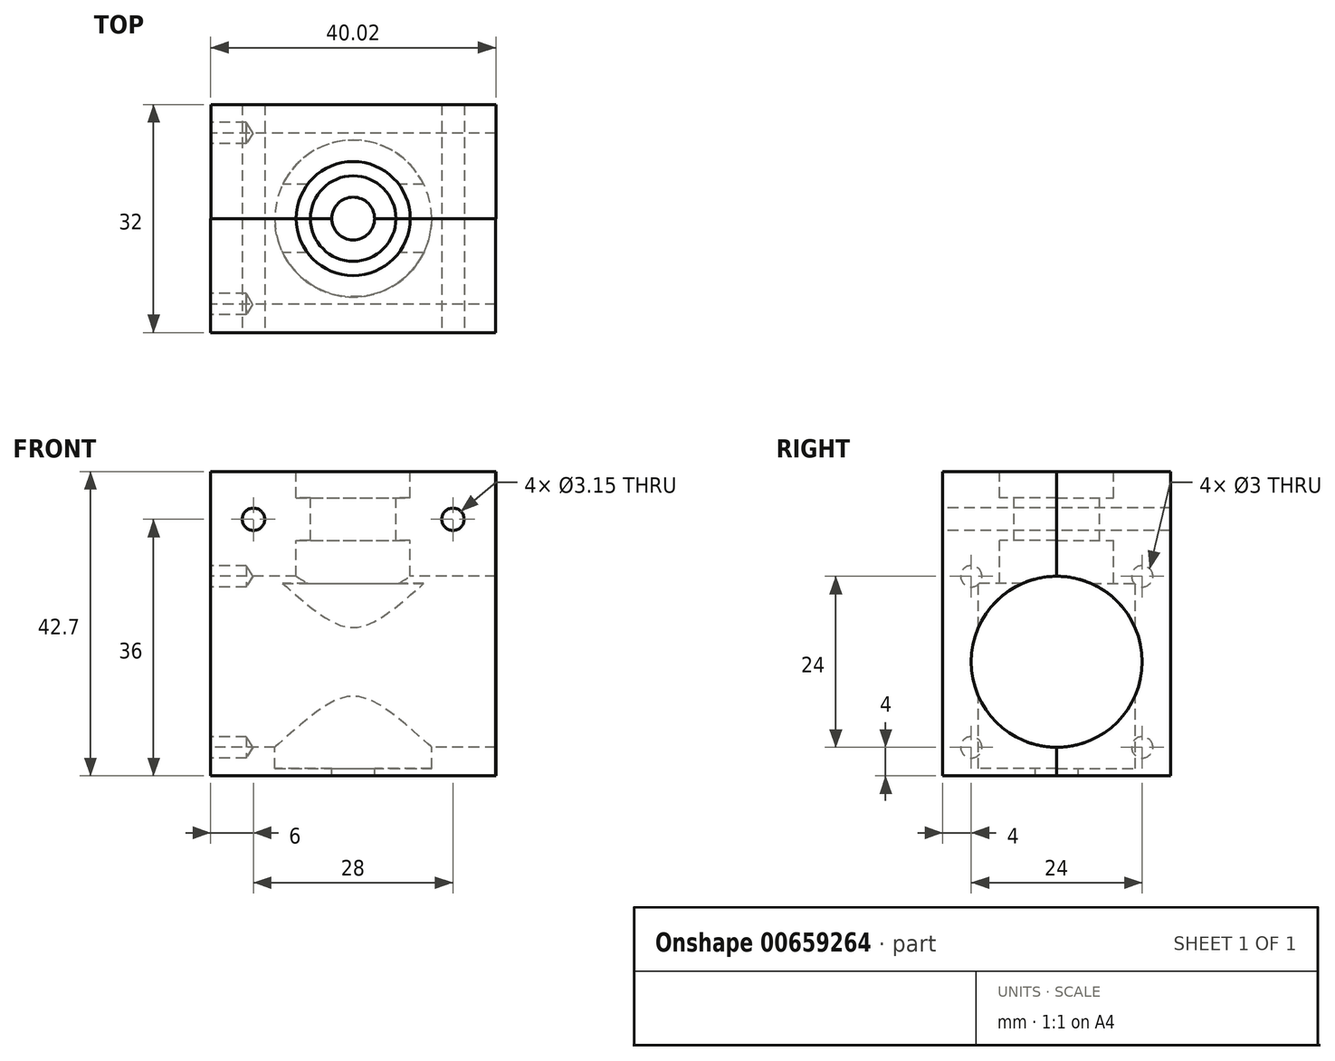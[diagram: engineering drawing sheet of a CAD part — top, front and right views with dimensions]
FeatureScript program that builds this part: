
annotation { "Feature Type Name" : "Feature", "Feature Type Description" : "" }
export const myFeature = defineFeature(function(context is Context, id is Id, definition is map)
    precondition{}
    {
        {
            var Q0;
            Q0=qCreatedBy(makeId("Top.planeOp"),FACE);
            var sketch = newSketch(context, id + "F0", { "sketchPlane" : qUnion([Q0])});
            skLineSegment(sketch, "E0.bottom", {"start": v(20, 8) * mm, "end": v(-20, 8) * mm});
            skLineSegment(sketch, "E0.top", {"start": v(20, -8) * mm, "end": v(-20, -8) * mm});
            skLineSegment(sketch, "E0.left", {"start": v(20, 8) * mm, "end": v(20, -8) * mm});
            skLineSegment(sketch, "E0.right", {"start": v(-20, 8) * mm, "end": v(-20, -8) * mm});
            skPoint(sketch, "E0.middle", {"position": v(0, 0) * mm});
            skSolve(sketch);
        }
        {
            var Q0;
            Q0=makeQuery(id+"F0.imprint","IMPRINT",FACE,{"disambiguationData":[TD([[makeQuery(id+"F0.imprint","IMPRINT",EDGE,{"derivedFrom":sQuery(id+"F0.wireOp",EDGE,"E0.bottom")}),1.0]])]});
            var sketch = newSketch(context, id + "F1", { "sketchPlane" : qUnion([Q0])});
            skLineSegment(sketch, "E1.bottom", {"start": v(-19.98, 8) * mm, "end": v(20.02, 8) * mm});
            skLineSegment(sketch, "E1.top", {"start": v(-19.98, 24) * mm, "end": v(20.02, 24) * mm});
            skLineSegment(sketch, "E1.left", {"start": v(-19.98, 8) * mm, "end": v(-19.98, 24) * mm});
            skLineSegment(sketch, "E1.right", {"start": v(20.02, 8) * mm, "end": v(20.02, 24) * mm});
            skSolve(sketch);
        }
        {
            var Q0;
            Q0=makeQuery(id+"F0.imprint","IMPRINT",FACE,{"disambiguationData":[TD([[makeQuery(id+"F0.imprint","IMPRINT",EDGE,{"derivedFrom":sQuery(id+"F0.wireOp",EDGE,"E0.bottom")}),1.0]])]});
            extrude(context, id + "F2", {"entities" : qUnion([Q0]), "depth" : 42.7 * mm, "offsetDistance" : 25 * mm});
        }
        {
            var Q0;
            Q0 = qSketchRegion(id + "F1", true);
            extrude(context, id + "F3", {"entities" : qUnion([Q0]), "depth" : 42.7 * mm, "offsetDistance" : 25 * mm});
        }
        {
            var Q0;
            Q0=makeQuery(id+"F2.opExtrude","CAP_FACE",FACE,{"disambiguationData":[OSD([sQuery(id+"F0.wireOp",EDGE,"E0.bottom"),sQuery(id+"F0.wireOp",EDGE,"E0.top"),sQuery(id+"F0.wireOp",EDGE,"E0.left"),sQuery(id+"F0.wireOp",EDGE,"E0.right")])],"isStart":false});
            var sketch = newSketch(context, id + "F4", { "sketchPlane" : qUnion([Q0])});
            skCircle(sketch, "E2", {"center": v(0, 8) * mm, "radius": 8 * mm});
            skSolve(sketch);
        }
        {
            var Q0;
            {var subQ0=sQuery(id+"F4.wireOp",EDGE,"E2");var subQ1=makeQuery(id+"F2.opExtrude","CAP_EDGE",EDGE,{"disambiguationData":[OSD([sQuery(id+"F0.wireOp",EDGE,"E0.bottom")])],"isStart":false});var subQ2=makeQuery(id+"F4.imprint","INTERSECT",VERTEX,{"disambiguationData":[OD(0.0)],"derivedFrom":[subQ1,subQ0]});Q0=makeQuery(id+"F4.imprint","IMPRINT",FACE,{"disambiguationData":[TD([[makeQuery(id+"F4.imprint","IMPRINT",EDGE,{"disambiguationData":[TD([[subQ2,1.0]])],"derivedFrom":subQ0}),1.0]])]});}
            var Q1;
            {var subQ0=sQuery(id+"F4.wireOp",EDGE,"E2");var subQ1=makeQuery(id+"F2.opExtrude","CAP_EDGE",EDGE,{"disambiguationData":[OSD([sQuery(id+"F0.wireOp",EDGE,"E0.bottom")])],"isStart":false});var subQ2=makeQuery(id+"F4.imprint","INTERSECT",VERTEX,{"disambiguationData":[OD(0.0)],"derivedFrom":[subQ1,subQ0]});Q1=makeQuery(id+"F4.imprint","IMPRINT",FACE,{"disambiguationData":[TD([[makeQuery(id+"F4.imprint","IMPRINT",EDGE,{"disambiguationData":[TD([[subQ2,-1.0]])],"derivedFrom":subQ0}),1.0]])]});}
            extrude(context, id + "F5", {"entities" : qUnion([Q0, Q1]), "operationType" : NewBodyOperationType.REMOVE, "oppositeDirection" : true, "depth" : 3.7 * mm, "offsetDistance" : 25 * mm});
        }
        {
            var Q0;
            Q0=makeQuery(id+"F5.boolean.opBoolean","COPY",FACE,{"derivedFrom":makeQuery(id+"F5.opExtrude","CAP_FACE",FACE,{"disambiguationData":[OSD([sQuery(id+"F0.wireOp",EDGE,"E0.bottom"),sQuery(id+"F4.wireOp",EDGE,"E2")])],"isStart":false})});
            var sketch = newSketch(context, id + "F6", { "sketchPlane" : qUnion([Q0])});
            skCircle(sketch, "E3", {"center": v(0, 8) * mm, "radius": 6 * mm});
            skSolve(sketch);
        }
        {
            var Q0;
            Q0=qSketchRegion(id+"F6",true);
            extrude(context, id + "F7", {"entities" : qUnion([Q0]), "operationType" : NewBodyOperationType.REMOVE, "oppositeDirection" : true, "depth" : 6 * mm, "offsetDistance" : 25 * mm});
        }
        {
            var Q0;
            Q0=makeQuery(id+"F7.boolean.opBoolean","COPY",FACE,{"derivedFrom":makeQuery(id+"F7.opExtrude","CAP_FACE",FACE,{"disambiguationData":[OSD([sQuery(id+"F6.wireOp",EDGE,"E3")])],"isStart":false})});
            var sketch = newSketch(context, id + "F8", { "sketchPlane" : qUnion([Q0])});
            skCircle(sketch, "E4", {"center": v(0, 8) * mm, "radius": 8 * mm});
            skSolve(sketch);
        }
        {
            var Q0;
            Q0=qSketchRegion(id+"F8",true);
            extrude(context, id + "F9", {"entities" : qUnion([Q0]), "operationType" : NewBodyOperationType.REMOVE, "oppositeDirection" : true, "depth" : 6 * mm, "offsetDistance" : 25 * mm});
        }
        {
            var Q0;
            Q0=makeQuery(id+"F9.boolean.opBoolean","COPY",FACE,{"derivedFrom":makeQuery(id+"F9.opExtrude","CAP_FACE",FACE,{"disambiguationData":[OSD([sQuery(id+"F8.wireOp",EDGE,"E4")])],"isStart":false})});
            var sketch = newSketch(context, id + "F10", { "sketchPlane" : qUnion([Q0])});
            skCircle(sketch, "E5", {"center": v(0, 8) * mm, "radius": 11 * mm});
            skSolve(sketch);
        }
        {
            var Q0;
            Q0 = qSketchRegion(id + "F10", true);
            extrude(context, id + "F11", {"entities" : qUnion([Q0]), "operationType" : NewBodyOperationType.REMOVE, "oppositeDirection" : true, "depth" : 26 * mm, "offsetDistance" : 25 * mm});
        }
        {
            var Q0;
            Q0=makeQuery(id+"F11.boolean.opBoolean","COPY",FACE,{"derivedFrom":makeQuery(id+"F11.opExtrude","CAP_FACE",FACE,{"disambiguationData":[OSD([sQuery(id+"F10.wireOp",EDGE,"E5")])],"isStart":false})});
            var sketch = newSketch(context, id + "F12", { "sketchPlane" : qUnion([Q0])});
            skCircle(sketch, "E6", {"center": v(0, 8) * mm, "radius": 3 * mm});
            skSolve(sketch);
        }
        {
            var Q0;
            Q0 = qSketchRegion(id + "F12", true);
            extrude(context, id + "F13", {"entities" : qUnion([Q0]), "operationType" : NewBodyOperationType.REMOVE, "oppositeDirection" : true, "depth" : 1 * mm, "offsetDistance" : 25 * mm});
        }
        {
            var Q0;
            Q0=makeQuery(id+"F2.opExtrude","SWEPT_FACE",FACE,{"disambiguationData":[OSD([sQuery(id+"F0.wireOp",EDGE,"E0.right")])]});
            var sketch = newSketch(context, id + "F14", { "sketchPlane" : qUnion([Q0])});
            skSolve(sketch);
        }
        {
            var Q0;
            {var subQ0=sQuery(id+"F0.wireOp",EDGE,"E0.right");Q0=makeQuery(id+"F14.imprint","IMPRINT",FACE,{"disambiguationData":[TD([[makeQuery(id+"F14.imprint","IMPRINT",EDGE,{"derivedFrom":makeQuery(id+"F2.opExtrude","CAP_EDGE",EDGE,{"disambiguationData":[OSD([subQ0])],"isStart":true})}),1.0]])]});}
            var sketch = newSketch(context, id + "F15", { "sketchPlane" : qUnion([Q0])});
            skPoint(sketch, "E7", {"position": v(4, 4) * mm});
            skSolve(sketch);
        }
        {
            var Q0;
            Q0=sQuery(id+"F15.wireOp",VERTEX,"E7");
            var Q1;
            Q1=makeQuery(id+"F2.opExtrude","SWEPT_BODY",BODY,{"disambiguationData":[OSD([sQuery(id+"F0.wireOp",EDGE,"E0.bottom"),sQuery(id+"F0.wireOp",EDGE,"E0.top"),sQuery(id+"F0.wireOp",EDGE,"E0.left"),sQuery(id+"F0.wireOp",EDGE,"E0.right")])]});
            hole(context, id + "F16", {"style" : HoleStyle.SIMPLE, "endStyle" : HoleEndStyle.BLIND, "holeDiameter" : 3 * mm, "majorDiameter" : 5 * mm, "holeDepth" : 5 * mm, "isTappedThrough" : true, "tappedDepth" : 12 * mm, "tapClearance" : 3, "locations" : qUnion([Q0]), "scope" : qUnion([Q1])});
        }
        {
            var Q0;
            Q0=makeQuery(id+"F3.opExtrude","SWEPT_FACE",FACE,{"disambiguationData":[OSD([sQuery(id+"F1.wireOp",EDGE,"E1.left")])]});
            var sketch = newSketch(context, id + "F17", { "sketchPlane" : qUnion([Q0])});
            skPoint(sketch, "E8", {"position": v(-20, 4) * mm});
            skPoint(sketch, "E9", {"position": v(-20, 28) * mm});
            skSolve(sketch);
        }
        {
            var Q0;
            Q0=sQuery(id+"F17.wireOp",VERTEX,"E8");
            var Q1;
            Q1=makeQuery(id+"F3.opExtrude","SWEPT_BODY",BODY,{"disambiguationData":[OSD([sQuery(id+"F1.wireOp",EDGE,"E1.bottom"),sQuery(id+"F1.wireOp",EDGE,"E1.top"),sQuery(id+"F1.wireOp",EDGE,"E1.left"),sQuery(id+"F1.wireOp",EDGE,"E1.right")])]});
            hole(context, id + "F18", {"style" : HoleStyle.SIMPLE, "endStyle" : HoleEndStyle.BLIND, "holeDiameter" : 3 * mm, "majorDiameter" : 5 * mm, "holeDepth" : 5 * mm, "isTappedThrough" : true, "tappedDepth" : 12 * mm, "tapClearance" : 3, "locations" : qUnion([Q0]), "scope" : qUnion([Q1])});
        }
        {
            var Q0;
            {var subQ0=sQuery(id+"F0.wireOp",EDGE,"E0.right");Q0=makeQuery(id+"F14.imprint","IMPRINT",FACE,{"disambiguationData":[TD([[makeQuery(id+"F14.imprint","IMPRINT",EDGE,{"derivedFrom":makeQuery(id+"F2.opExtrude","CAP_EDGE",EDGE,{"disambiguationData":[OSD([subQ0])],"isStart":true})}),1.0]])]});}
            var sketch = newSketch(context, id + "F19", { "sketchPlane" : qUnion([Q0])});
            skPoint(sketch, "E10", {"position": v(4, 28) * mm});
            skSolve(sketch);
        }
        {
            var Q0;
            Q0=sQuery(id+"F19.wireOp",VERTEX,"E10");
            var Q1;
            Q1=makeQuery(id+"F2.opExtrude","SWEPT_BODY",BODY,{"disambiguationData":[OSD([sQuery(id+"F0.wireOp",EDGE,"E0.bottom"),sQuery(id+"F0.wireOp",EDGE,"E0.top"),sQuery(id+"F0.wireOp",EDGE,"E0.left"),sQuery(id+"F0.wireOp",EDGE,"E0.right")])]});
            hole(context, id + "F20", {"style" : HoleStyle.SIMPLE, "endStyle" : HoleEndStyle.BLIND, "holeDiameter" : 3 * mm, "majorDiameter" : 5 * mm, "holeDepth" : 5 * mm, "isTappedThrough" : true, "tappedDepth" : 12 * mm, "tapClearance" : 3, "locations" : qUnion([Q0]), "scope" : qUnion([Q1])});
        }
        {
            var Q0;
            Q0=makeQuery(id+"F3.opExtrude","SWEPT_FACE",FACE,{"disambiguationData":[OSD([sQuery(id+"F1.wireOp",EDGE,"E1.left")])]});
            var sketch = newSketch(context, id + "F21", { "sketchPlane" : qUnion([Q0])});
            skPoint(sketch, "E11", {"position": v(-20, 28) * mm});
            skSolve(sketch);
        }
        {
            var Q0;
            Q0=sQuery(id+"F21.wireOp",VERTEX,"E11");
            var Q1;
            Q1=makeQuery(id+"F3.opExtrude","SWEPT_BODY",BODY,{"disambiguationData":[OSD([sQuery(id+"F1.wireOp",EDGE,"E1.bottom"),sQuery(id+"F1.wireOp",EDGE,"E1.top"),sQuery(id+"F1.wireOp",EDGE,"E1.left"),sQuery(id+"F1.wireOp",EDGE,"E1.right")])]});
            hole(context, id + "F22", {"style" : HoleStyle.SIMPLE, "endStyle" : HoleEndStyle.BLIND, "holeDiameter" : 3 * mm, "majorDiameter" : 5 * mm, "holeDepth" : 5 * mm, "isTappedThrough" : true, "tappedDepth" : 12 * mm, "tapClearance" : 3, "locations" : qUnion([Q0]), "scope" : qUnion([Q1])});
        }
        {
            var Q0;
            Q0=makeQuery(id+"F2.opExtrude","SWEPT_FACE",FACE,{"disambiguationData":[OSD([sQuery(id+"F0.wireOp",EDGE,"E0.top")])]});
            var sketch = newSketch(context, id + "F23", { "sketchPlane" : qUnion([Q0])});
            skPoint(sketch, "E12", {"position": v(-14, 36) * mm});
            skPoint(sketch, "E13", {"position": v(14, 36) * mm});
            skSolve(sketch);
        }
        {
            var Q0;
            Q0=sQuery(id+"F23.wireOp",VERTEX,"E12");
            var Q1;
            Q1=makeQuery(id+"F2.opExtrude","SWEPT_BODY",BODY,{"disambiguationData":[OSD([sQuery(id+"F0.wireOp",EDGE,"E0.bottom"),sQuery(id+"F0.wireOp",EDGE,"E0.top"),sQuery(id+"F0.wireOp",EDGE,"E0.left"),sQuery(id+"F0.wireOp",EDGE,"E0.right")])]});
            var Q2;
            Q2=makeQuery(id+"F3.opExtrude","SWEPT_BODY",BODY,{"disambiguationData":[OSD([sQuery(id+"F1.wireOp",EDGE,"E1.bottom"),sQuery(id+"F1.wireOp",EDGE,"E1.top"),sQuery(id+"F1.wireOp",EDGE,"E1.left"),sQuery(id+"F1.wireOp",EDGE,"E1.right")])]});
            hole(context, id + "F24", {"style" : HoleStyle.SIMPLE, "endStyle" : HoleEndStyle.THROUGH, "standardTappedOrClearance" : lookupTablePath({ "standard" : "ISO", "fit" : "Close", "size" : "M3", "type" : "Clearance" }), "standardBlindInLast" : lookupTablePath({ "fit" : "Close", "standard" : "ISO", "size" : "M3", "type" : "Clearance" }), "holeDiameter" : 3.15 * mm, "majorDiameter" : 5 * mm, "isTappedThrough" : true, "tappedDepth" : 12 * mm, "tapClearance" : 3, "locations" : qUnion([Q0]), "scope" : qUnion([Q1, Q2])});
        }
        {
            var Q0;
            Q0=makeQuery(id+"F2.opExtrude","SWEPT_FACE",FACE,{"disambiguationData":[OSD([sQuery(id+"F0.wireOp",EDGE,"E0.top")])]});
            var sketch = newSketch(context, id + "F25", { "sketchPlane" : qUnion([Q0])});
            skPoint(sketch, "E14", {"position": v(14, 36) * mm});
            skSolve(sketch);
        }
        {
            var Q0;
            Q0=sQuery(id+"F25.wireOp",VERTEX,"E14");
            var Q1;
            Q1=makeQuery(id+"F2.opExtrude","SWEPT_BODY",BODY,{"disambiguationData":[OSD([sQuery(id+"F0.wireOp",EDGE,"E0.bottom"),sQuery(id+"F0.wireOp",EDGE,"E0.top"),sQuery(id+"F0.wireOp",EDGE,"E0.left"),sQuery(id+"F0.wireOp",EDGE,"E0.right")])]});
            var Q2;
            Q2=makeQuery(id+"F3.opExtrude","SWEPT_BODY",BODY,{"disambiguationData":[OSD([sQuery(id+"F1.wireOp",EDGE,"E1.bottom"),sQuery(id+"F1.wireOp",EDGE,"E1.top"),sQuery(id+"F1.wireOp",EDGE,"E1.left"),sQuery(id+"F1.wireOp",EDGE,"E1.right")])]});
            hole(context, id + "F26", {"style" : HoleStyle.SIMPLE, "endStyle" : HoleEndStyle.THROUGH, "standardTappedOrClearance" : lookupTablePath({ "standard" : "ISO", "fit" : "Close", "size" : "M3", "type" : "Clearance" }), "standardBlindInLast" : lookupTablePath({ "fit" : "Close", "standard" : "ISO", "size" : "M3", "type" : "Clearance" }), "holeDiameter" : 3.15 * mm, "majorDiameter" : 5 * mm, "isTappedThrough" : true, "tappedDepth" : 12 * mm, "tapClearance" : 3, "locations" : qUnion([Q0]), "scope" : qUnion([Q1, Q2])});
        }
        {
            var Q0;
            {var subQ0=sQuery(id+"F0.wireOp",EDGE,"E0.right");Q0=makeQuery(id+"F14.imprint","IMPRINT",FACE,{"disambiguationData":[TD([[makeQuery(id+"F14.imprint","IMPRINT",EDGE,{"derivedFrom":makeQuery(id+"F2.opExtrude","CAP_EDGE",EDGE,{"disambiguationData":[OSD([subQ0])],"isStart":true})}),1.0]])]});}
            var sketch = newSketch(context, id + "F27", { "sketchPlane" : qUnion([Q0])});
            skPoint(sketch, "E15", {"position": v(-8, 16) * mm});
            skSolve(sketch);
        }
        {
            var Q0;
            Q0=sQuery(id+"F27.wireOp",VERTEX,"E15");
            var Q1;
            Q1=makeQuery(id+"F2.opExtrude","SWEPT_BODY",BODY,{"disambiguationData":[OSD([sQuery(id+"F0.wireOp",EDGE,"E0.bottom"),sQuery(id+"F0.wireOp",EDGE,"E0.top"),sQuery(id+"F0.wireOp",EDGE,"E0.left"),sQuery(id+"F0.wireOp",EDGE,"E0.right")])]});
            var Q2;
            Q2=makeQuery(id+"F3.opExtrude","SWEPT_BODY",BODY,{"disambiguationData":[OSD([sQuery(id+"F1.wireOp",EDGE,"E1.bottom"),sQuery(id+"F1.wireOp",EDGE,"E1.top"),sQuery(id+"F1.wireOp",EDGE,"E1.left"),sQuery(id+"F1.wireOp",EDGE,"E1.right")])]});
            hole(context, id + "F28", {"style" : HoleStyle.SIMPLE, "endStyle" : HoleEndStyle.THROUGH, "holeDiameter" : 24 * mm, "majorDiameter" : 5 * mm, "isTappedThrough" : true, "tappedDepth" : 12 * mm, "tapClearance" : 3, "locations" : qUnion([Q0]), "scope" : qUnion([Q1, Q2])});
        }
    });
